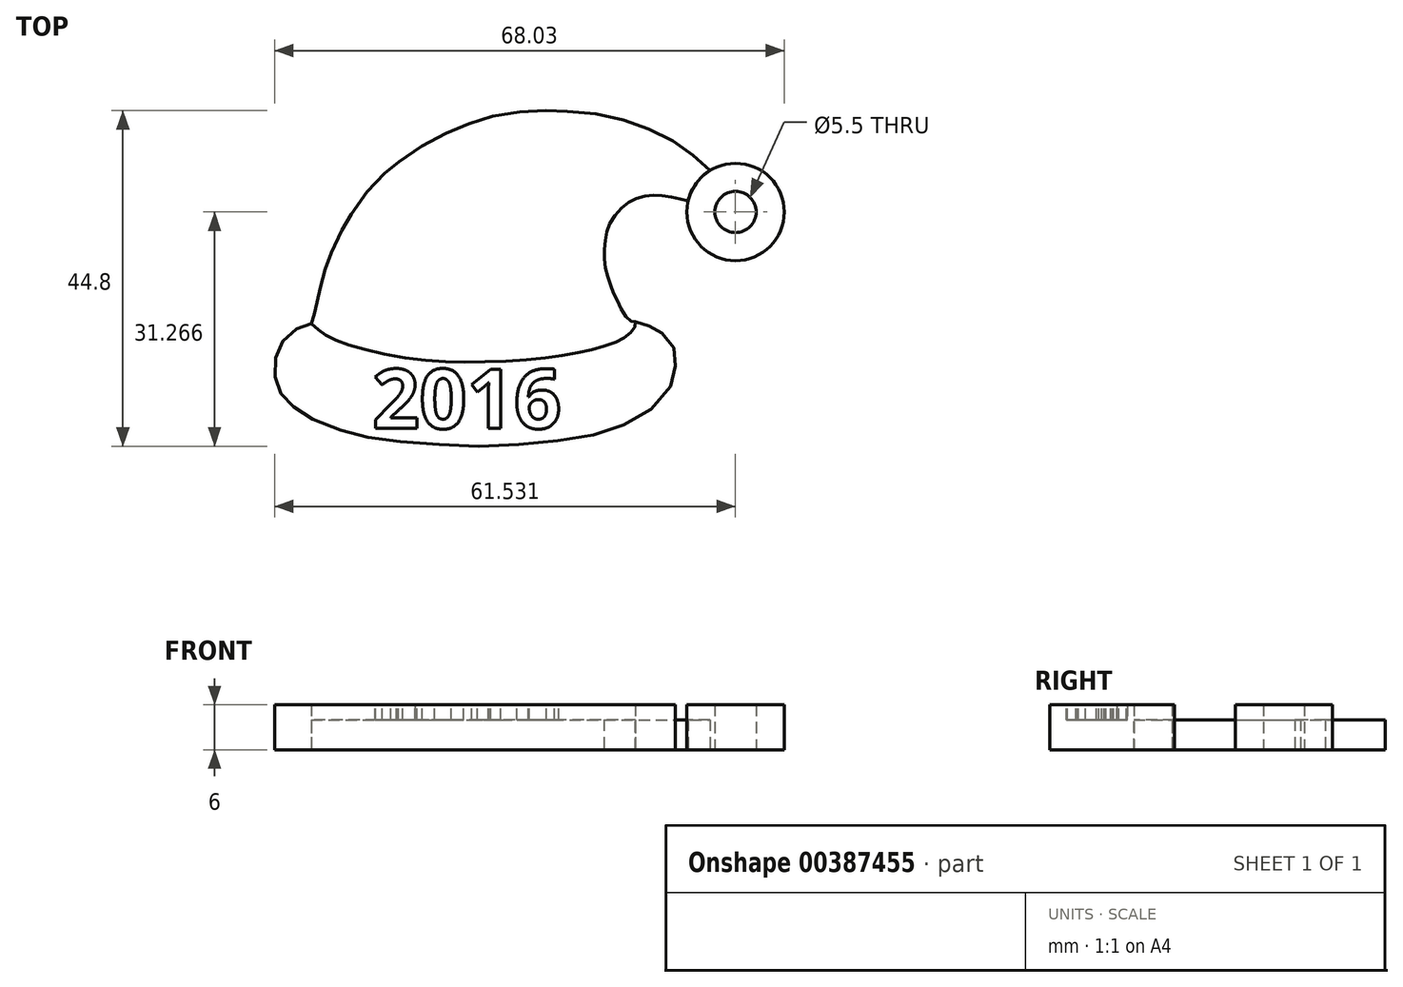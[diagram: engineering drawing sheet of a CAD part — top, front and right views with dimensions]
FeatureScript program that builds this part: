
annotation { "Feature Type Name" : "Feature", "Feature Type Description" : "" }
export const myFeature = defineFeature(function(context is Context, id is Id, definition is map)
    precondition{}
    {
        {
            var Q0;
            Q0=qCreatedBy(makeId("Top.planeOp"),FACE);
            var sketch = newSketch(context, id + "F0", { "sketchPlane" : qUnion([Q0])});
            skFitSpline(sketch, "E0", {"points": [v(9.88, 19.07) * mm, v(8.92, 18.83) * mm, v(7.4, 18.03) * mm, v(6.13, 16.8) * mm, v(5.46, 15.56) * mm, v(5.02, 13.57) * mm, v(5.1, 11.77) * mm, v(5.58, 10.3) * mm, v(6.5, 8.94) * mm, v(8, 7.63) * mm, v(10.44, 6.2) * mm, v(14.82, 4.56) * mm, v(18.81, 3.68) * mm, v(25.72, 3.02) * mm, v(33.82, 2.73) * mm, v(41.84, 3.35) * mm, v(48.43, 4.44) * mm, v(53.07, 6.29) * mm, v(57.1, 9.42) * mm, v(58.38, 12.64) * mm, v(58.48, 13.92) * mm, v(58.33, 15.72) * mm, v(57.24, 17.38) * mm, v(56.2, 18.14) * mm, v(55.2, 18.66) * mm, v(54.07, 19.14) * mm, v(53.17, 19.37) * mm], "startDerivative": vector(-39.02, -7.46) * mm, "endDerivative": vector(-38.74, 8.7) * mm});
            skFitSpline(sketch, "E1", {"points": [v(53.17, 19.37) * mm, v(53.17, 18.96) * mm, v(53, 18.48) * mm, v(52.56, 17.89) * mm, v(51.76, 17.27) * mm, v(50.82, 16.75) * mm, v(49.03, 16.08) * mm, v(46.58, 15.44) * mm, v(43.42, 14.86) * mm, v(38.96, 14.32) * mm, v(32.93, 13.99) * mm, v(27.5, 14.05) * mm, v(21.8, 14.62) * mm, v(16.23, 15.86) * mm, v(13.39, 16.77) * mm, v(11.68, 17.64) * mm, v(10.84, 18.24) * mm, v(9.88, 19.07) * mm], "startDerivative": vector(1.1, -16.48) * mm, "endDerivative": vector(-22.85, 20.23) * mm});
            skCircle(sketch, "E2", {"center": v(66.52, 33.99) * mm, "radius": 6.5 * mm});
            skFitSpline(sketch, "E3", {"points": [v(53.17, 19.37) * mm, v(52.7, 19.37) * mm, v(51.85, 20.08) * mm, v(50.9, 21.82) * mm, v(50.18, 23.36) * mm, v(49.56, 25.14) * mm, v(49.09, 27) * mm, v(49.02, 29.05) * mm, v(49.3, 31.06) * mm, v(49.87, 32.71) * mm, v(51.37, 34.6) * mm, v(52.95, 35.68) * mm, v(54.74, 36.16) * mm, v(56.47, 36.18) * mm, v(58.56, 35.88) * mm, v(60.2, 35.47) * mm], "startDerivative": vector(-13.01, -2.26) * mm, "endDerivative": vector(23.85, -6.45) * mm});
            skFitSpline(sketch, "E4", {"points": [v(9.88, 19.07) * mm, v(10.15, 19.24) * mm, v(10.26, 19.9) * mm, v(10.38, 20.6) * mm, v(10.6, 21.57) * mm, v(10.8, 22.44) * mm, v(11.1, 23.75) * mm, v(11.47, 25.31) * mm, v(12.12, 27.44) * mm, v(12.64, 28.72) * mm, v(14.13, 31.85) * mm, v(15, 33.3) * mm, v(16.97, 36.17) * mm, v(19.56, 39.02) * mm, v(20.7, 39.9) * mm, v(23.24, 41.92) * mm, v(27, 44.04) * mm, v(30.06, 45.42) * mm, v(33.18, 46.5) * mm, v(36.84, 47.22) * mm, v(40.82, 47.52) * mm, v(43.03, 47.46) * mm, v(47.03, 47.2) * mm, v(51.35, 46.35) * mm, v(55, 45.02) * mm, v(58.5, 43.3) * mm, v(61.04, 41.42) * mm, v(63.13, 39.53) * mm], "startDerivative": vector(23.5, 7.6) * mm, "endDerivative": vector(50.98, -47.51) * mm});
            skSolve(sketch);
        }
        {
            var Q0;
            Q0=makeQuery(id+"F0.imprint","IMPRINT",FACE,{"disambiguationData":[TD([[makeQuery(id+"F0.imprint","IMPRINT",EDGE,{"derivedFrom":sQuery(id+"F0.wireOp",EDGE,"E0")}),1.0]])]});
            var Q1;
            {var subQ0=sQuery(id+"F0.wireOp",EDGE,"E2");var subQ1=makeQuery(id+"F0.imprint","INTERSECT",VERTEX,{"derivedFrom":[subQ0,sQuery(id+"F0.wireOp",EDGE,"E3")]});Q1=makeQuery(id+"F0.imprint","IMPRINT",FACE,{"disambiguationData":[TD([[makeQuery(id+"F0.imprint","IMPRINT",EDGE,{"disambiguationData":[TD([[subQ1,1.0]])],"derivedFrom":subQ0}),1.0]])]});}
            extrude(context, id + "F1", {"entities" : qUnion([Q0, Q1]), "depth" : 6 * mm});
        }
        {
            var Q0;
            Q0=makeQuery(id+"F0.imprint","IMPRINT",FACE,{"disambiguationData":[TD([[makeQuery(id+"F0.imprint","IMPRINT",EDGE,{"derivedFrom":sQuery(id+"F0.wireOp",EDGE,"E1")}),-1.0]])]});
            extrude(context, id + "F2", {"entities" : qUnion([Q0]), "depth" : 4 * mm});
        }
        {
            var Q0;
            Q0=makeQuery(id+"F1.opExtrude","CAP_FACE",FACE,{"disambiguationData":[OSD([sQuery(id+"F0.wireOp",EDGE,"E0"),sQuery(id+"F0.wireOp",EDGE,"E1")])],"isStart":false});
            var sketch = newSketch(context, id + "F3", { "sketchPlane" : qUnion([Q0])});
            skText(sketch, "E5", { "text": "2016\n", "fontName": "OpenSans-Bold.ttf"});
            const initialGuessF3  = {"E5": [0.01802, 0.0051, 1, 0, 0.00796]};
            skSetInitialGuess(sketch, initialGuessF3);
            skSolve(sketch);
        }
        {
            var Q0;
            Q0 = qSketchRegion(id + "F3", true);
            extrude(context, id + "F4", {"entities" : qUnion([Q0]), "operationType" : NewBodyOperationType.REMOVE, "oppositeDirection" : true, "depth" : 2 * mm});
        }
        {
            var Q0;
            Q0=sQuery(id+"F0.wireOp",VERTEX,"E2.center");
            var Q1;
            Q1=makeQuery(id+"F1.opExtrude","SWEPT_BODY",BODY,{"disambiguationData":[OSD([sQuery(id+"F0.wireOp",EDGE,"E2")])]});
            hole(context, id + "F5", {"style" : HoleStyle.SIMPLE, "endStyle" : HoleEndStyle.THROUGH, "oppositeDirection" : true, "holeDiameter" : 5.5 * mm, "isTappedThrough" : true, "tappedDepth" : 12 * mm, "tapClearance" : 3, "locations" : qUnion([Q0]), "scope" : qUnion([Q1])});
        }
    });
